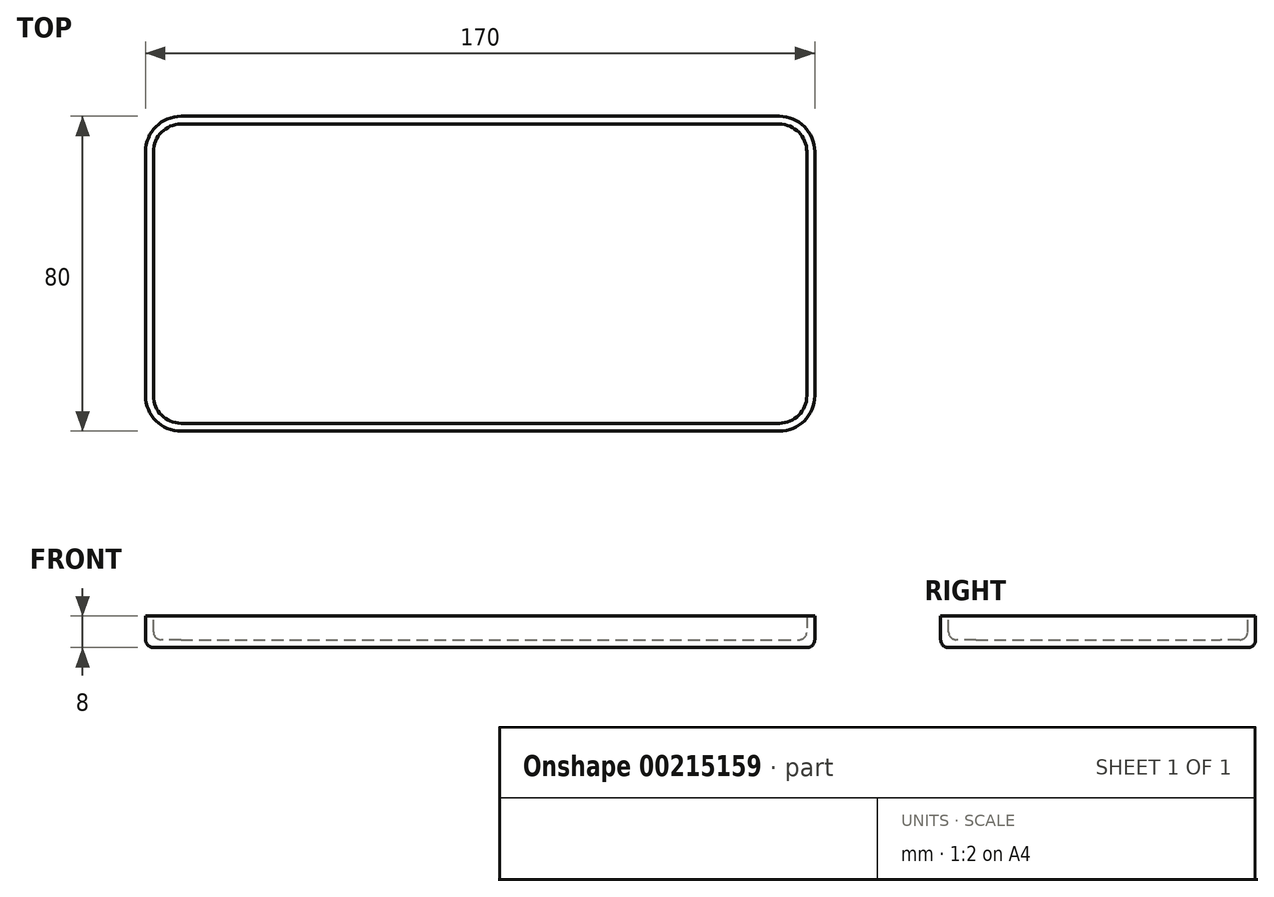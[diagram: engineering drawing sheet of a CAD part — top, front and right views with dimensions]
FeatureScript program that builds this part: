
annotation { "Feature Type Name" : "Feature", "Feature Type Description" : "" }
export const myFeature = defineFeature(function(context is Context, id is Id, definition is map)
    precondition{}
    {
        {
            var Q0;
            Q0=qCreatedBy(makeId("Top.planeOp"),FACE);
            var sketch = newSketch(context, id + "F0", { "sketchPlane" : qUnion([Q0])});
            skLineSegment(sketch, "E0.bottom", {"start": v(-76, -40) * mm, "end": v(76, -40) * mm});
            skLineSegment(sketch, "E0.top", {"start": v(-76, 40) * mm, "end": v(76, 40) * mm});
            skLineSegment(sketch, "E0.left", {"start": v(-85, -31) * mm, "end": v(-85, 31) * mm});
            skLineSegment(sketch, "E0.right", {"start": v(85, -31) * mm, "end": v(85, 31) * mm});
            skPoint(sketch, "E0.middle", {"position": v(0, 0) * mm});
            skPoint(sketch, "E1.visualSharp", {"position": v(-85, 40) * mm});
            skArc(sketch, "E1.filletArc", {"start": v(-76, 40) * mm, "mid": v(-82.36, 37.36) * mm, "end": v(-85, 31) * mm});
            skPoint(sketch, "E2.visualSharp", {"position": v(85, 40) * mm});
            skArc(sketch, "E2.filletArc", {"start": v(85, 31) * mm, "mid": v(82.36, 37.36) * mm, "end": v(76, 40) * mm});
            skPoint(sketch, "E3.visualSharp", {"position": v(85, -40) * mm});
            skArc(sketch, "E3.filletArc", {"start": v(76, -40) * mm, "mid": v(82.36, -37.36) * mm, "end": v(85, -31) * mm});
            skPoint(sketch, "E4.visualSharp", {"position": v(-85, -40) * mm});
            skArc(sketch, "E4.filletArc", {"start": v(-85, -31) * mm, "mid": v(-82.36, -37.36) * mm, "end": v(-76, -40) * mm});
            skSolve(sketch);
        }
        {
            var Q0;
            Q0=makeQuery(id+"F0.imprint","IMPRINT",FACE,{"disambiguationData":[TD([[makeQuery(id+"F0.imprint","IMPRINT",EDGE,{"derivedFrom":sQuery(id+"F0.wireOp",EDGE,"E0.bottom")}),1.0]])]});
            extrude(context, id + "F1", {"entities" : qUnion([Q0]), "depth" : 8 * mm});
        }
        {
            var Q0;
            Q0=makeQuery(id+"F1.opExtrude","CAP_FACE",FACE,{"disambiguationData":[OSD([sQuery(id+"F0.wireOp",EDGE,"E0.bottom"),sQuery(id+"F0.wireOp",EDGE,"E0.top"),sQuery(id+"F0.wireOp",EDGE,"E0.left"),sQuery(id+"F0.wireOp",EDGE,"E0.right"),sQuery(id+"F0.wireOp",EDGE,"E1.filletArc"),sQuery(id+"F0.wireOp",EDGE,"E2.filletArc"),sQuery(id+"F0.wireOp",EDGE,"E3.filletArc"),sQuery(id+"F0.wireOp",EDGE,"E4.filletArc")])],"isStart":false});
            shell(context, id + "F2", {"entities" : qUnion([Q0]), "thickness" : 2 * mm});
        }
        {
            var Q0;
            {var subQ0=sQuery(id+"F0.wireOp",EDGE,"E0.top");Q0=makeQuery(id+"F2.opShell","OFFSET_EDGE",EDGE,{"disambiguationData":[OSD([subQ0]),TDD([makeQuery(id+"F1.opExtrude","CAP_EDGE",EDGE,{"disambiguationData":[OSD([subQ0])],"isStart":true})])]});}
            fillet(context, id + "F3", {"entities" : qUnion([Q0]), "radius" : 2 * mm, "tangentPropagation" : true, "allowEdgeOverflow" : false});
        }
        {
            var Q0;
            Q0=makeQuery(id+"F1.opExtrude","CAP_EDGE",EDGE,{"disambiguationData":[OSD([sQuery(id+"F0.wireOp",EDGE,"E0.bottom")])],"isStart":true});
            fillet(context, id + "F4", {"entities" : qUnion([Q0]), "radius" : 2 * mm, "tangentPropagation" : true, "allowEdgeOverflow" : false});
        }
        {
            var Q0;
            Q0=qCreatedBy(makeId("Front.planeOp"),FACE);
            var sketch = newSketch(context, id + "F5", { "sketchPlane" : qUnion([Q0])});
            skPoint(sketch, "E5", {"position": v(-83, 2) * mm});
            skSolve(sketch);
        }
    });
